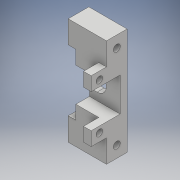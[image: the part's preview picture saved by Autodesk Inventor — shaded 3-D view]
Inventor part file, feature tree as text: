
AUTODESK INVENTOR PART (.ipt)
format: ipt  version: 2017 (Build 210142000, 142)  size: 434,176 bytes
history: native  units: mm
features: extrude x19, sketch x19, projected_geometry x8
ambient origin geometry x8: Origin, YZ Plane, XZ Plane, XY Plane, X Axis, Y Axis, Z Axis, Center Point
bodies: Solide1 (feature_tree)
feature tree (46):
  extrude  "Extrusion1"  Depth=5.0mm
  extrude  "Extrusion2"  Depth=5.0mm
  extrude  "Extrusion3"  Depth=110.0mm
  extrude  "Extrusion4"  Depth=9.0mm
  extrude  "Extrusion5"  Depth=110.0mm
  sketch  "Esquisse8"
  extrude  "Extrusion6"  Depth=40.148494mm
  extrude  "Extrusion7"  Depth=9.0mm
  extrude  "Extrusion8"  Depth=15.0mm TaperAngle=0.0deg
  extrude  "Extrusion9"  Depth=12.0mm
  extrude  "Extrusion10"  Depth=15.0mm TaperAngle=0.0deg
  extrude  "Extrusion11"  Depth=3.8mm
  extrude  "Extrusion12"  Depth=60.0mm
  extrude  "Extrusion13"  Depth=15.0mm TaperAngle=0.0deg
  extrude  "Extrusion14"  Depth=16.2mm
  extrude  "Extrusion15"  Depth=30.0mm TaperAngle=0.0deg
  extrude  "Extrusion16"  Depth=10.0mm
  extrude  "Extrusion17"  Depth=16.0mm
  extrude  "Extrusion18"  Depth=8.0mm
  extrude  "Extrusion19"  Depth=8.0mm
  sketch  "Esquisse1"
  sketch  "Esquisse4"
  sketch  "Esquisse5"
  sketch  "Esquisse6"
  sketch  "Esquisse7"
  projected_geometry  "Boucle projetée1"
  projected_geometry  "Boucle projetée2"
  sketch  "Esquisse10"
  sketch  "Esquisse13"
  sketch  "Esquisse14"
  sketch  "Esquisse15"
  sketch  "Esquisse16"
  projected_geometry  "Boucle projetée5"
  sketch  "Esquisse17"
  projected_geometry  "Boucle projetée6"
  projected_geometry  "Boucle projetée7"
  sketch  "Esquisse18"
  projected_geometry  "Boucle projetée8"
  sketch  "Esquisse21"
  sketch  "Esquisse22"
  sketch  "Esquisse23"
  sketch  "Esquisse24"
  projected_geometry  "Boucle projetée10"
  projected_geometry  "Boucle projetée11"
  sketch  "Esquisse26"
  sketch  "Esquisse28"
